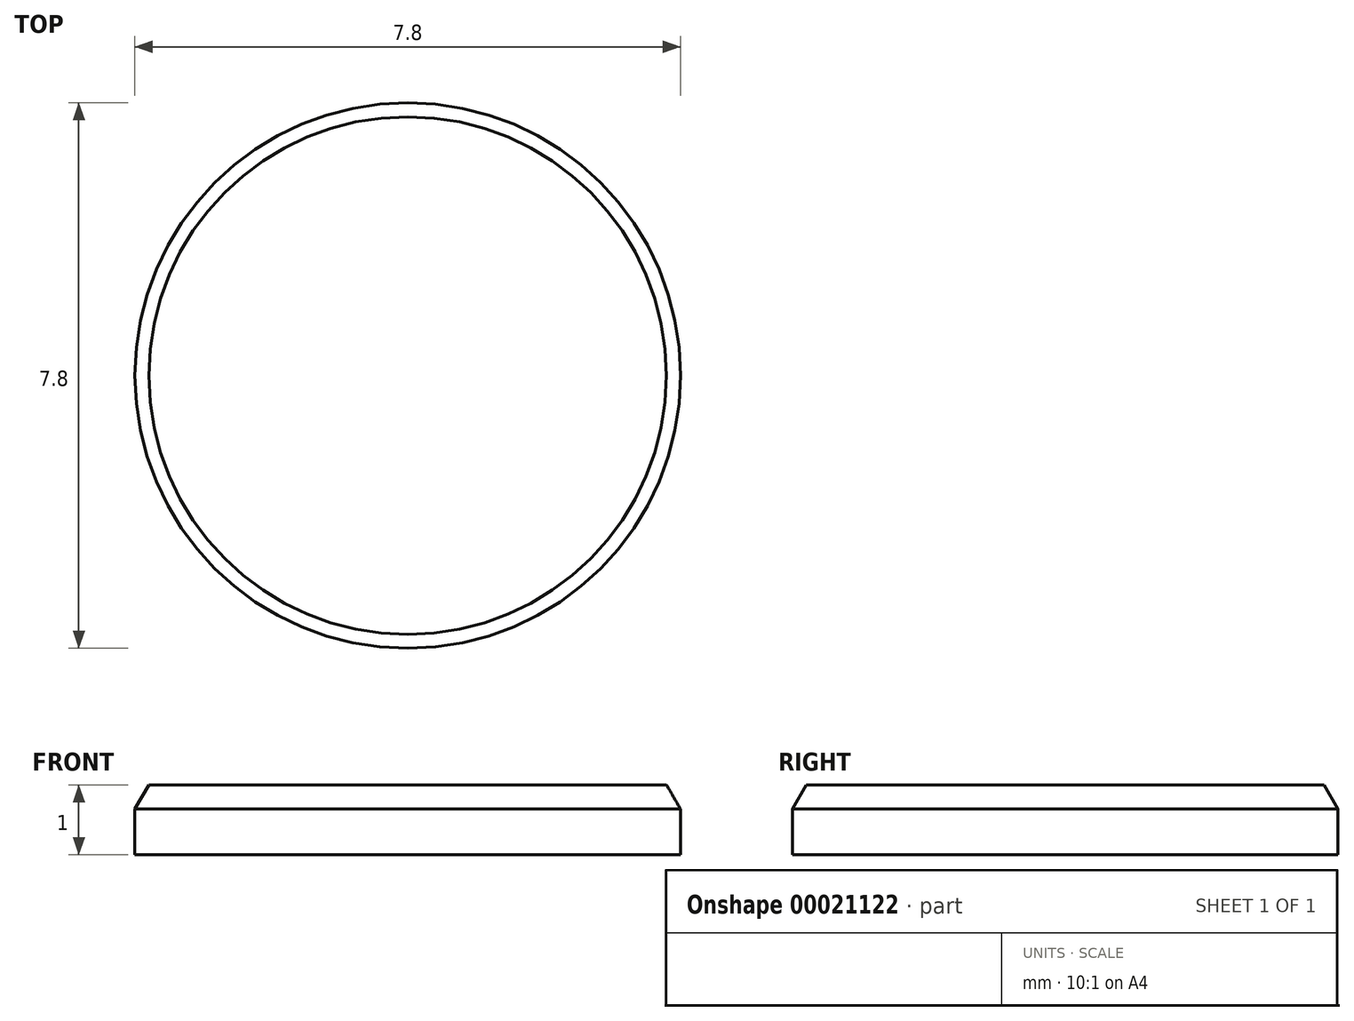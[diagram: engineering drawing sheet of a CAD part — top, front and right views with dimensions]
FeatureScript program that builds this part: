
annotation { "Feature Type Name" : "Feature", "Feature Type Description" : "" }
export const myFeature = defineFeature(function(context is Context, id is Id, definition is map)
    precondition{}
    {
        {
            var Q0;
            Q0=qCreatedBy(makeId("Top.planeOp"),FACE);
            var sketch = newSketch(context, id + "F0", { "sketchPlane" : qUnion([Q0])});
            skCircle(sketch, "E0", {"center": v(0, 0) * mm, "radius": 3.9 * mm});
            skSolve(sketch);
        }
        {
            var Q0;
            Q0 = qSketchRegion(id + "F0", true);
            extrude(context, id + "F1", {"entities" : qUnion([Q0]), "depth" : 1 * mm});
        }
        {
            var Q0;
            Q0=makeQuery(id+"F1.opExtrude","CAP_EDGE",EDGE,{"disambiguationData":[OSD([sQuery(id+"F0.wireOp",EDGE,"E0")])],"isStart":false});
            chamfer(context, id + "F2", {"entities" : qUnion([Q0]), "chamferType" : ChamferType.OFFSET_ANGLE, "width" : 0.2 * mm, "oppositeDirection" : false, "angle" : 60 * degree, "tangentPropagation" : true});
        }
    });
